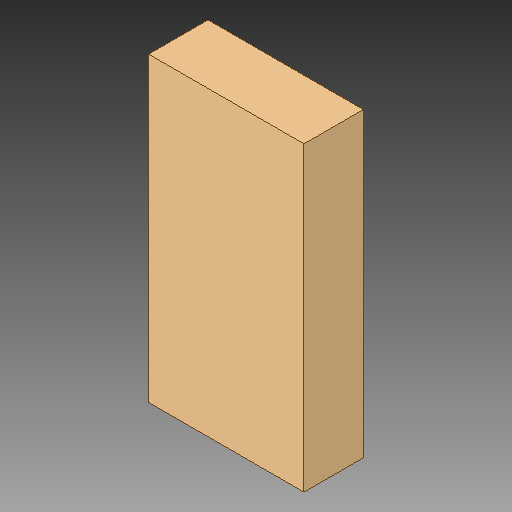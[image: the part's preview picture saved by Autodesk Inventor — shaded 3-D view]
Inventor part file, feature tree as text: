
AUTODESK INVENTOR PART (.ipt)
format: ipt  version: 2018 (Build 220112000, 112)  size: 79,872 bytes
history: native  units: in
note: dims shown in document units (in); Inventor stores cm internally (conversion verified against a paired STEP export)
features: other x1, extrude x1
ambient origin geometry x8: Origin, YZ Plane, XZ Plane, XY Plane, X Axis, Y Axis, Z Axis, Center Point
bodies: Solid1 (feature_tree)
feature tree (2):
  other  "JP1M, TXD_71"
  extrude  "Extrusion1"  Depth=0.0394in TaperAngle=0.0deg
